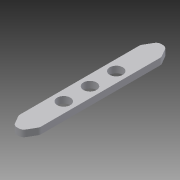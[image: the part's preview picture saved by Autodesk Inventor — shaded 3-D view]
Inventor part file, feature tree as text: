
AUTODESK INVENTOR PART (.ipt)
format: ipt  version: 2014 (Build 180170000, 170)  size: 131,072 bytes
history: native  units: in
note: dims shown in document units (in); Inventor stores cm internally (conversion verified against a paired STEP export)
features: chamfer x4, sketch x2, extrude x1, hole x1, pattern_linear x1, fillet x1
ambient origin geometry x8: Origin, YZ Plane, XZ Plane, XY Plane, X Axis, Y Axis, Z Axis, Center Point
bodies: Solid1 (feature_tree)
feature tree (10):
  extrude  "Extrusion1"  TaperAngle=0.0deg  [1 undecoded]
  hole  "Hole1"  [1 undecoded]
  pattern_linear  "Rectangular Pattern1"  Spacing1=0.125in  [1 undecoded]
  chamfer  "Chamfer2"  Distance=0.0625in Angle=60.0deg
  chamfer  "Chamfer3"  Distance=0.0625in Angle=60.0deg
  chamfer  "Chamfer4"  Distance=0.0625in Angle=60.0deg
  chamfer  "Chamfer5"  Distance=0.0625in
  fillet  "Fillet1"  [1 undecoded]
  sketch  "Sketch1"  dims[d2=0.0625in d3=0.0in]
  sketch  "Sketch2"  dims[d6=0.125in d7=0.75in d8=0.375in d9=0.25in d10=0.5635in d11=1.0in d12=0.8108in d13=1.1811in d15=0.25in d20=0.125in d22=0.0625in d23=0.125in d24=60.0deg d25=0.0625in d26=0.125in d27=60.0deg d28=0.0625in d29=0.125in d30=60.0deg d31=0.0625in]
note: 4 required parameter values undecoded (feature->parameter linkage not recoverable at this tier; creation-order binding heuristic only, values carry confidence <= 0.55)
